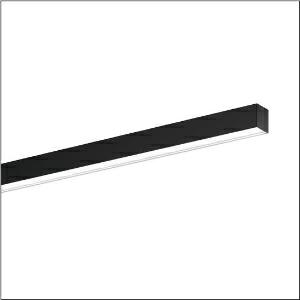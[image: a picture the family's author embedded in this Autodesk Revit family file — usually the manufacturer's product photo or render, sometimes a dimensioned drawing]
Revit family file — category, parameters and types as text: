
# Revit family: silica_r__21_51mx20db42bb_5dab
name_source: partatom
category: Lighting Fixtures
units: mm (PartAtom-declared; Revit-internal decimal feet)

## family parameters
Cut with Voids When Loaded = No
Host = Face
Light Source = No
Part Type = Normal
Room Calculation Point = No
Round Connector Dimension = Use Diameter
Shared = No

## types (1)
- --- (1 x LED, 3000 lm, 19 W, 4000K)
    Apparent Load = 19 VA
    CIE Flux Codes = 48 79 96 100 100
    Color Rendering = 80
    Color Temperature = 4000K
    Default Elevation = 1800 mm
    Description = Silica® 21, office luminaire, primary optical cover: cover, of PMMA, opal, light emission: direct distribution, primary light characteristic: symmetric, installation type: surface-mounted, LED, rated luminous flux: 3.000lm, luminous efficacy: 158lm/W, light colour: 840, colour temperature: 4000K, with terminal, 3+2-pole, max. 2.5mm², mains connection: 220..240V, AC, 50/60Hz, rated input power: 19W, luminaire housing, of aluminium, jet black (RAL 9005), length: 1.504mm, width: 53mm, height: 53mm, protection rating (complete): IP20, insulation class (complete): insulation class I (protective earthing), certification: CE, permissible operating ambient temperature: 0..+35°C, standard: EN 50419, packaging unit: 1 piece
    Height = 0 mm  [stored 0 ft]
    Lamp = 1 x LED
    Lamp Light Flux = 3000 lm
    Lamp Power = 19 W
    Lamp count = 1
    Length = 1504 mm
    Luminous efficacy = 158 lm/W
    Manufacturer = Siteco
    ModVariant = No
    Model = 51MX20DB42BB
    Mounting Place = Ceiling
    Mounting Type = Recessed
    Number of Poles = 1
    OnlyDefault = Yes
    Power Factor = 1
    Product Name = Silica® 21
    Product group = office luminaire | ceiling recessed
    ProductGroupID = 400
    Protection Class = Protection class I
    Protection Degree = IP 20
    RLX_Detail_Level = 1
    RLX_Emergency_Light_Flux = 0 lm
    RLX_Emergency_Type = 0
    RLX_Emergency_Type_DB = No
    RlxData = <blob elided: 28793 chars, md5=ca6321d9>
    Socket = socket
    Standby Power = 0 W
    System Light Flux = 3000 lm
    System Power = 19 W
    Type Comments = factory setting: luminous flux: 100 % | dim-lin: 254 | 218 mA
    Type Image = l_1335925.jpg
    URL = http://relux.com
    VarID = @adj_087097
    Voltage = 0 V
    Weight = 0.00 kg
    Width = 53 mm

note: [stored X ft] marks values corroborated as IEEE doubles in the binary element streams (Revit-internal decimal feet)

## geometry (parser evidence)
native form markers: Blend x4, Sweep x11
no freeform markers — native parametric forms only
